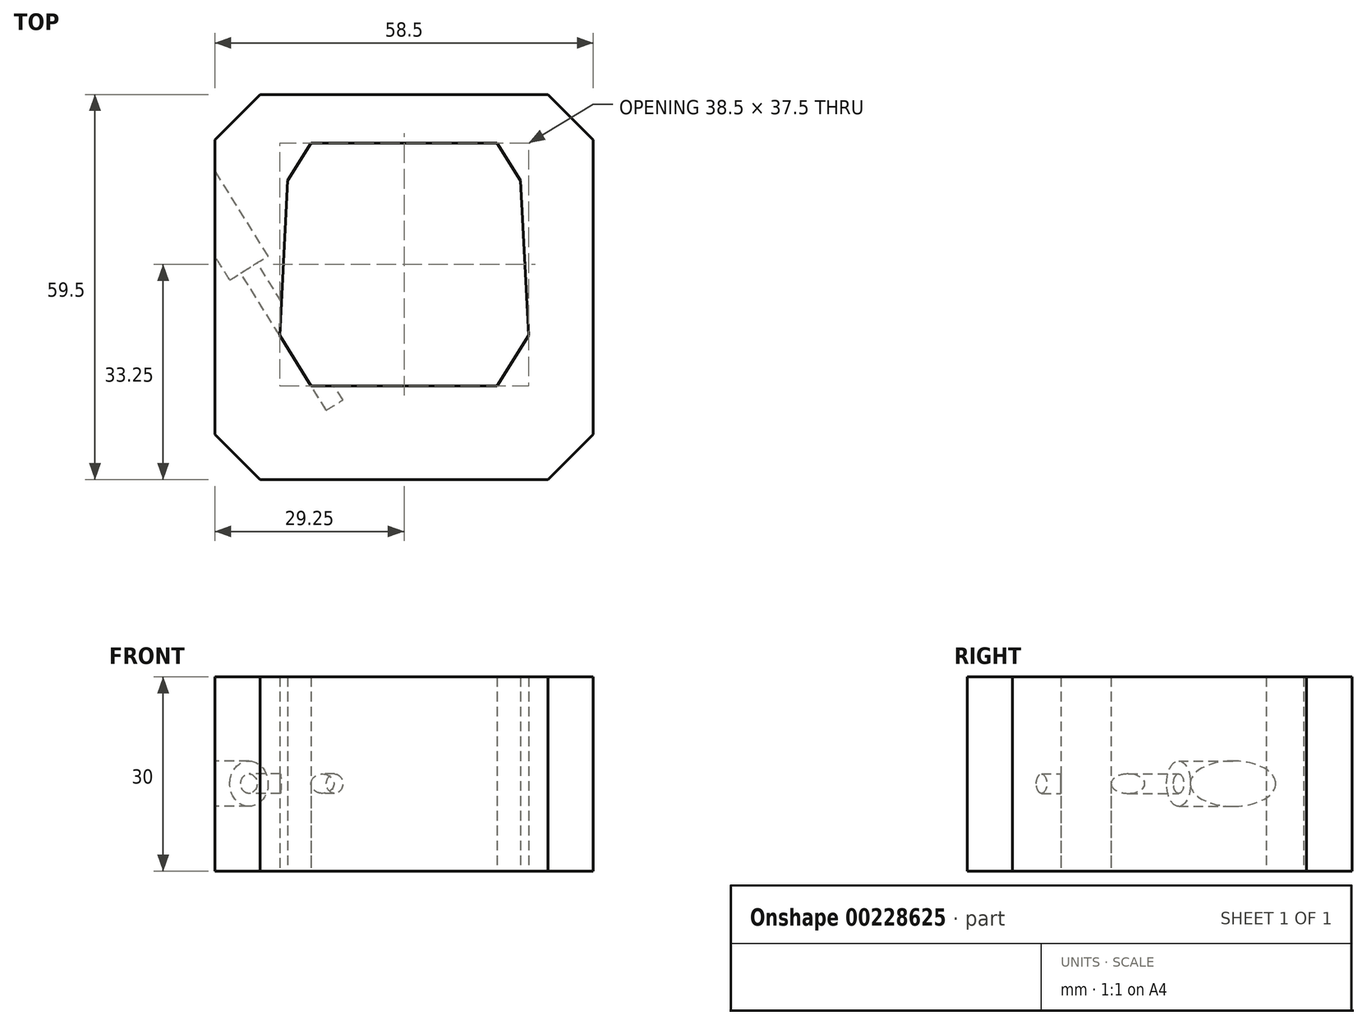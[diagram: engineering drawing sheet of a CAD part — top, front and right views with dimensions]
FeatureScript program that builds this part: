
annotation { "Feature Type Name" : "Feature", "Feature Type Description" : "" }
export const myFeature = defineFeature(function(context is Context, id is Id, definition is map)
    precondition{}
    {
        {
            var Q0;
            Q0=qCreatedBy(makeId("Top.planeOp"),FACE);
            var sketch = newSketch(context, id + "F0", { "sketchPlane" : qUnion([Q0])});
            skLineSegment(sketch, "E0", {"start": v(-14.4, -18.75) * mm, "end": v(14.4, -18.75) * mm});
            skLineSegment(sketch, "E1", {"start": v(14.4, -18.75) * mm, "end": v(19.25, -10.98) * mm});
            skLineSegment(sketch, "E2", {"start": v(19.25, -10.98) * mm, "end": v(18, 12.99) * mm});
            skLineSegment(sketch, "E3", {"start": v(18, 12.99) * mm, "end": v(14.4, 18.75) * mm});
            skLineSegment(sketch, "E4", {"start": v(14.4, 18.75) * mm, "end": v(-14.4, 18.75) * mm});
            skLineSegment(sketch, "E5", {"start": v(-14.4, 18.75) * mm, "end": v(-18, 12.99) * mm});
            skLineSegment(sketch, "E6", {"start": v(-18, 12.99) * mm, "end": v(-19.25, -10.98) * mm});
            skLineSegment(sketch, "E7", {"start": v(-19.25, -10.98) * mm, "end": v(-14.4, -18.75) * mm});
            skLineSegment(sketch, "E8", {"start": v(-22.25, -33.25) * mm, "end": v(22.25, -33.25) * mm});
            skLineSegment(sketch, "E9", {"start": v(22.25, -33.25) * mm, "end": v(29.25, -26.25) * mm});
            skLineSegment(sketch, "E10", {"start": v(29.25, -26.25) * mm, "end": v(29.25, 19.25) * mm});
            skLineSegment(sketch, "E11", {"start": v(29.25, 19.25) * mm, "end": v(22.25, 26.25) * mm});
            skLineSegment(sketch, "E12", {"start": v(22.25, 26.25) * mm, "end": v(-22.25, 26.25) * mm});
            skLineSegment(sketch, "E13", {"start": v(-22.25, 26.25) * mm, "end": v(-29.25, 19.25) * mm});
            skLineSegment(sketch, "E14", {"start": v(-29.25, 19.25) * mm, "end": v(-29.25, -26.25) * mm});
            skLineSegment(sketch, "E15", {"start": v(-29.25, -26.25) * mm, "end": v(-22.25, -33.25) * mm});
            skSolve(sketch);
        }
        {
            var Q0;
            Q0=makeQuery(id+"F0.imprint","IMPRINT",FACE,{"disambiguationData":[TD([[makeQuery(id+"F0.imprint","IMPRINT",EDGE,{"derivedFrom":sQuery(id+"F0.wireOp",EDGE,"E0")}),-1.0]])]});
            extrude(context, id + "F1", {"entities" : qUnion([Q0]), "depth" : 30 * mm});
        }
        {
            var Q0;
            Q0=qCreatedBy(makeId("Top.planeOp"),FACE);
            cPlane(context, id + "F2", {"entities" : qUnion([Q0]), "cplaneType" : CPlaneType.OFFSET, "offset" : 13.5 * mm, "width" : 150 * mm, "height" : 150 * mm});
        }
        {
            var Q0;
            Q0=qCreatedBy(id+"F2.planeOp",FACE);
            var sketch = newSketch(context, id + "F3", { "sketchPlane" : qUnion([Q0])});
            skLineSegment(sketch, "E16.0", {"start": v(-19.25, -10.98) * mm, "end": v(-14.4, -18.75) * mm, "construction": true});
            skLineSegment(sketch, "E17.0", {"start": v(-29.25, 19.25) * mm, "end": v(-29.25, -26.25) * mm, "construction": true});
            skLineSegment(sketch, "E18.0", {"start": v(-22.25, -33.25) * mm, "end": v(22.25, -33.25) * mm, "construction": true});
            skLineSegment(sketch, "E19", {"start": v(-34.06, 15.55) * mm, "end": v(-3.56, -33.25) * mm, "construction": true});
            skLineSegment(sketch, "E20", {"start": v(-10.75, -21.75) * mm, "end": v(-12.02, -22.54) * mm});
            skLineSegment(sketch, "E21", {"start": v(-12.02, -22.54) * mm, "end": v(-25.27, -1.34) * mm});
            skLineSegment(sketch, "E22", {"start": v(-25.27, -1.34) * mm, "end": v(-26.97, -2.4) * mm});
            skLineSegment(sketch, "E23", {"start": v(-26.97, -2.4) * mm, "end": v(-37.03, 13.7) * mm});
            skLineSegment(sketch, "E24.0", {"start": v(-22.25, 26.25) * mm, "end": v(-29.25, 19.25) * mm, "construction": true});
            skLineSegment(sketch, "E25", {"start": v(-37.03, 13.7) * mm, "end": v(-34.06, 15.55) * mm});
            skLineSegment(sketch, "E26", {"start": v(-34.06, 15.55) * mm, "end": v(-31.1, 17.4) * mm, "construction": true});
            skLineSegment(sketch, "E27", {"start": v(-10.75, -21.75) * mm, "end": v(-34.06, 15.55) * mm});
            skSolve(sketch);
        }
        {
            var Q0;
            Q0=makeQuery(id+"F3.imprint","IMPRINT",FACE,{"disambiguationData":[TD([[makeQuery(id+"F3.imprint","IMPRINT",EDGE,{"derivedFrom":sQuery(id+"F3.wireOp",EDGE,"E20")}),-1.0]])]});
            var Q1;
            Q1=sQuery(id+"F3.wireOp",EDGE,"E19");
            revolve(context, id + "F4", {"operationType" : NewBodyOperationType.REMOVE, "entities" : qUnion([Q0]), "axis" : qUnion([Q1]), "revolveType" : RevolveType.FULL});
        }
    });
